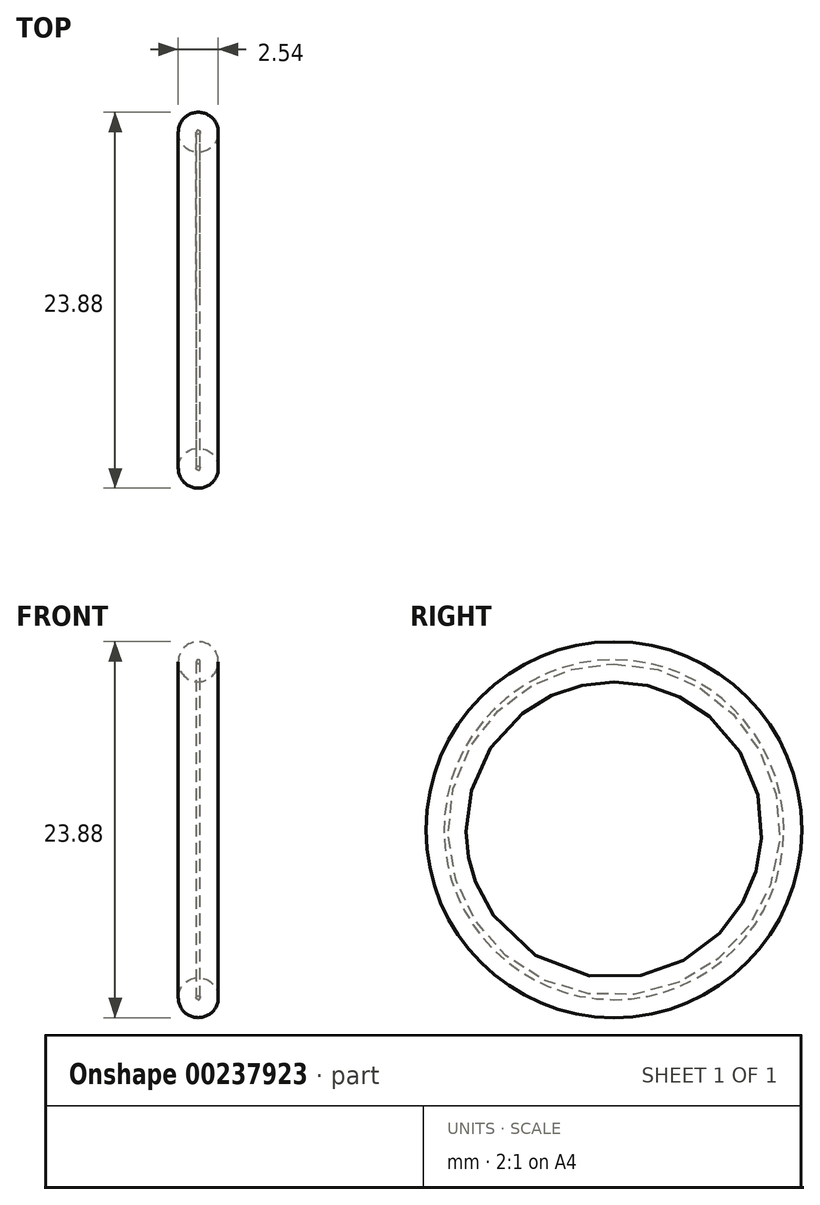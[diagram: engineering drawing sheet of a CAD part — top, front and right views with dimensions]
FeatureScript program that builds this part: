
annotation { "Feature Type Name" : "Feature", "Feature Type Description" : "" }
export const myFeature = defineFeature(function(context is Context, id is Id, definition is map)
    precondition{}
    {
        {
            var Q0;
            Q0=qCreatedBy(makeId("Front.planeOp"),FACE);
            var sketch = newSketch(context, id + "F0", { "sketchPlane" : qUnion([Q0])});
            skLineSegment(sketch, "E0", {"start": v(-16, 0) * mm, "end": v(19.42, 0) * mm});
            skCircle(sketch, "E1", {"center": v(0, 10.67) * mm, "radius": 0.13 * mm});
            skCircle(sketch, "E2", {"center": v(0, 10.67) * mm, "radius": 1.27 * mm});
            skLineSegment(sketch, "E3", {"start": v(0, 9.4) * mm, "end": v(0, 0) * mm});
            skSolve(sketch);
        }
        {
            var Q0;
            Q0 = qSketchRegion(id + "F0", true);
            var Q1;
            Q1=sQuery(id+"F0.wireOp",EDGE,"E0");
            revolve(context, id + "F1", {"entities" : qUnion([Q0]), "axis" : qUnion([Q1]), "revolveType" : RevolveType.FULL});
        }
    });
